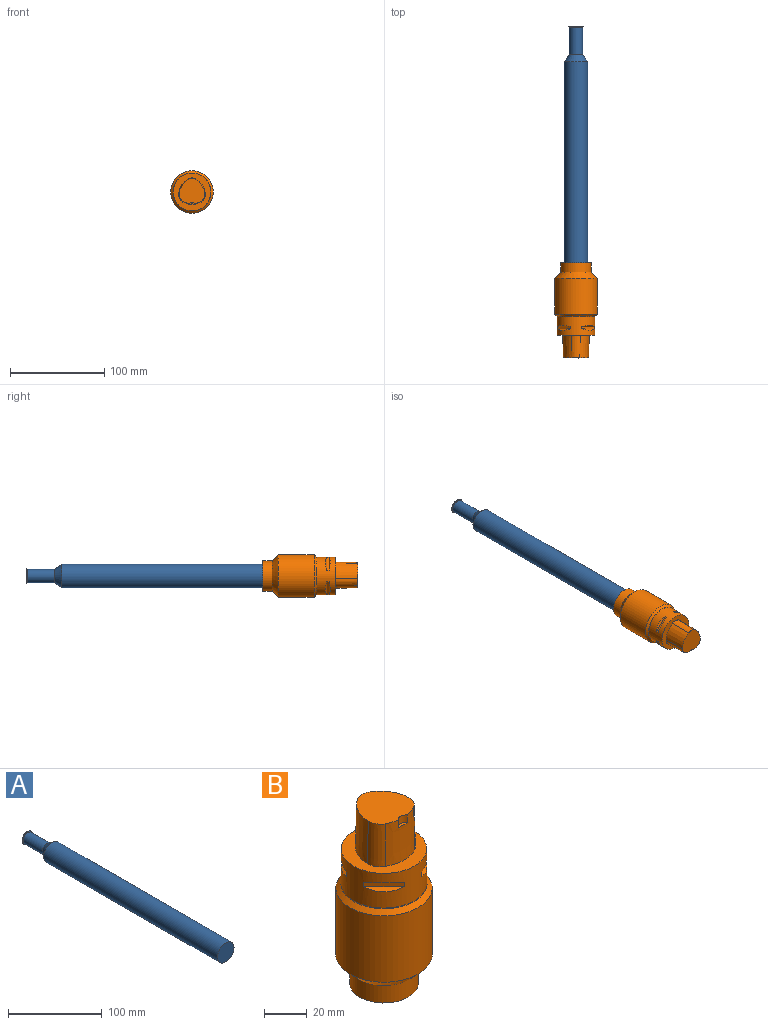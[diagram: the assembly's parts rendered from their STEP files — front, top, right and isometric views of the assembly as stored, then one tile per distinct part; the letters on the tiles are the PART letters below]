
ASSEMBLY  parts=2 mates=1
PART A: 7 faces, bbox 25x300x25 mm
  f0: cylinder r=12.5mm len=262.21mm, axis (0,1,0), area 20593.6mm2, adj f1,f2
  f1: plane 25x25mm, normal (0,-1,0), area 490.9mm2, adj f0
  f2: cone r=7mm half-angle=36.2deg, axis (0,-1,0), area 570mm2, adj f0,f5
  f3: cone r=8mm half-angle=60deg, axis (0,1,0), area 54.4mm2, adj f4,f5
  f4: cone r=8mm half-angle=60deg, axis (0,-1,0), area 61.1mm2, adj f3,f6
  f5: cylinder r=7mm len=29.06mm, axis (0,-1,0), area 1278.1mm2, adj f2,f3
  f6: plane 13.74x13.74mm, normal (0,1,0), area 148.2mm2, adj f4
PART B: 29 faces, bbox 45x45x101 mm
  f0: cylinder r=22.5mm len=45mm, axis (0,0,1), area 5372.1mm2, adj f24,f28
  f1: cone r=20mm half-angle=1.4deg, axis (0,0,-1), area 474.7mm2, adj f2,f6,f7,f8
  f2: cone r=8.5mm half-angle=1.4deg, axis (0,0,-1), area 214.7mm2, adj f1,f3,f7,f8
  f3: cone r=20mm half-angle=1.4deg, axis (0,0,-1), area 477.5mm2, adj f2,f4,f7,f8
  f4: cone r=8.5mm half-angle=1.4deg, axis (0,0,-1), area 214.7mm2, adj f3,f5,f7,f8
  f5: cone r=20mm half-angle=1.4deg, axis (0,0,-1), area 449.4mm2, adj f4,f6,f7,f8,f10,f11
  f6: cone r=8.5mm half-angle=1.4deg, axis (0,0,-1), area 213.4mm2, adj f1,f5,f7,f8
  f7: plane 26.86x26.61mm, normal (0,0,1), area 548.9mm2, adj f1,f2,f3,f4,f5,f6,f11
  f8: plane 40x40mm, normal (0,0,1), area 649.5mm2, adj f1,f2,f3,f4,f5,f6,f9
  f9: cylinder r=20mm len=40mm, axis (0,0,-1), area 2157.4mm2, adj f8,f12,f13,f14,f15,f16,f17,f18
  f10: plane 6.08x1.64mm, normal (0,0,1), area 6.9mm2, adj f5,f11
  f11: cylinder r=4mm len=6.08mm, axis (0,0,-1), area 28.5mm2, adj f5,f7,f10
  f12: plane 13.26x13.26mm, normal (-0.35,-0.35,0.87), area 34.1mm2, adj f9,f13
  f13: plane 13.26x13.26mm, normal (-0.71,-0.71,0), area 46.9mm2, adj f9,f12,f14
  f14: plane 13.26x13.26mm, normal (-0.35,-0.35,-0.87), area 34.1mm2, adj f9,f13
  f15: plane 13.26x13.26mm, normal (-0.35,0.35,0.87), area 34.1mm2, adj f9,f16
  f16: plane 13.26x13.26mm, normal (-0.71,0.71,0), area 46.9mm2, adj f9,f15,f17
  f17: plane 13.26x13.26mm, normal (-0.35,0.35,-0.87), area 34.1mm2, adj f9,f16
  f18: plane 13.26x13.26mm, normal (0.35,0.35,0.87), area 34.1mm2, adj f9,f19
  f19: plane 13.26x13.26mm, normal (0.71,0.71,0), area 46.9mm2, adj f9,f18,f20
  f20: plane 13.26x13.26mm, normal (0.35,0.35,-0.87), area 34.1mm2, adj f9,f19
  f21: plane 13.26x13.26mm, normal (0.35,-0.35,0.87), area 34.1mm2, adj f9,f22
  f22: plane 13.26x13.26mm, normal (0.71,-0.71,0), area 46.9mm2, adj f9,f21,f23
  f23: plane 13.26x13.26mm, normal (0.35,-0.35,-0.87), area 34.1mm2, adj f9,f22
  f24: cone r=22.5mm half-angle=45deg, axis (0,0,-1), area 451.2mm2, adj f0,f25
  f25: torus R=20.4mm, axis (0,0,1), area 39.6mm2, adj f9,f24
  f26: cylinder r=16mm len=32mm, axis (0,0,-1), area 1005.3mm2, adj f27,f28
  f27: plane 32x32mm, normal (0,0,-1), area 804.2mm2, adj f26
  f28: cone r=22.5mm half-angle=45deg, axis (0,0,1), area 1111.8mm2, adj f0,f26
PLACE A t=(-15.4,32.03,-67.77)mm
PLACE B rot(axis=(1,0,0),90deg) t=(-15.4,-296.29,-67.77)mm
MATE cylindrical B.f26 <-> A.f0  axis (0,1,0) through (-15.4,-219.29,-67.77)mm
